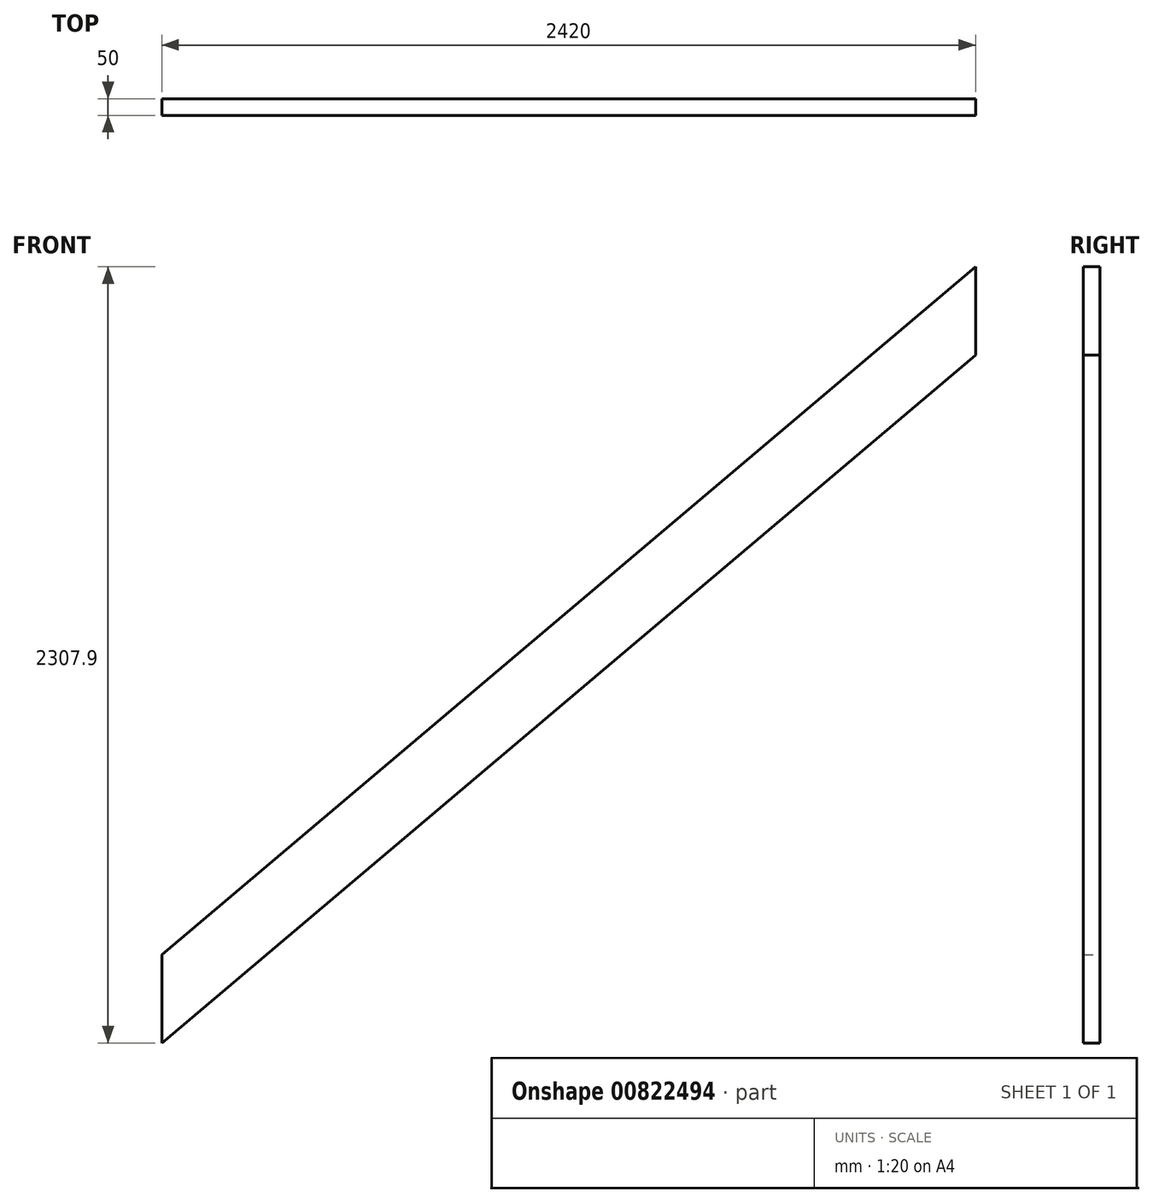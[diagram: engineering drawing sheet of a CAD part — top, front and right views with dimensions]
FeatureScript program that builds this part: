
annotation { "Feature Type Name" : "Feature", "Feature Type Description" : "" }
export const myFeature = defineFeature(function(context is Context, id is Id, definition is map)
    precondition{}
    {
        {
            var Q0;
            Q0=qCreatedBy(makeId("Front.planeOp"),FACE);
            var sketch = newSketch(context, id + "F0", { "sketchPlane" : qUnion([Q0])});
            skLineSegment(sketch, "E0", {"start": v(0, 0) * mm, "end": v(2420, 0) * mm, "construction": true});
            skLineSegment(sketch, "E1", {"start": v(2420, 0) * mm, "end": v(2420, 2046) * mm, "construction": true});
            skLineSegment(sketch, "E2", {"start": v(0, 0) * mm, "end": v(2420, 2046) * mm});
            skLineSegment(sketch, "E3", {"start": v(2420, 2307.9) * mm, "end": v(0, 261.9) * mm});
            skLineSegment(sketch, "E4", {"start": v(0, 0) * mm, "end": v(0, 261.9) * mm});
            skLineSegment(sketch, "E5", {"start": v(2420, 2046) * mm, "end": v(2420, 2307.9) * mm});
            skPoint(sketch, "E6.orphan", {"position": v(-309.77, 0) * mm});
            skSolve(sketch);
        }
        {
            var Q0;
            Q0 = qSketchRegion(id + "F0", true);
            extrude(context, id + "F1", {"entities" : qUnion([Q0]), "depth" : 50 * mm, "offsetDistance" : 25 * mm});
        }
    });
